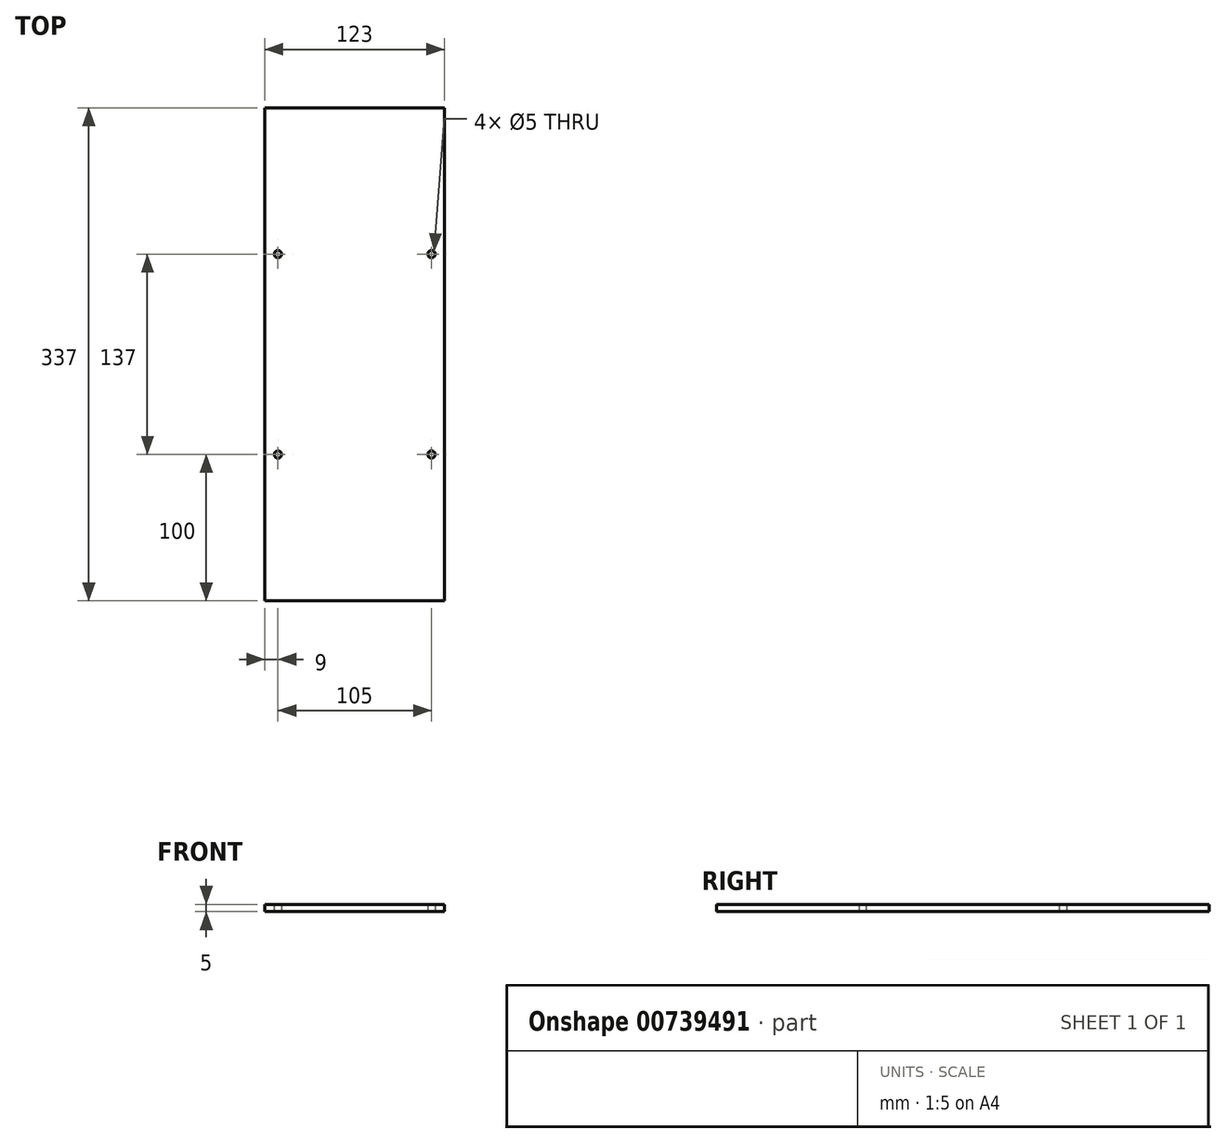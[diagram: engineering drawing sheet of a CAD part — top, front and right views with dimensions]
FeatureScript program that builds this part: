
annotation { "Feature Type Name" : "Feature", "Feature Type Description" : "" }
export const myFeature = defineFeature(function(context is Context, id is Id, definition is map)
    precondition{}
    {
        {
            var Q0;
            Q0=qCreatedBy(makeId("Top.planeOp"),FACE);
            var sketch = newSketch(context, id + "F0", { "sketchPlane" : qUnion([Q0])});
            skLineSegment(sketch, "E0.bottom", {"start": v(61.5, 168.5) * mm, "end": v(-61.5, 168.5) * mm});
            skLineSegment(sketch, "E0.top", {"start": v(61.5, -168.5) * mm, "end": v(-61.5, -168.5) * mm});
            skLineSegment(sketch, "E0.left", {"start": v(61.5, 168.5) * mm, "end": v(61.5, -168.5) * mm});
            skLineSegment(sketch, "E0.right", {"start": v(-61.5, 168.5) * mm, "end": v(-61.5, -168.5) * mm});
            skPoint(sketch, "E0.middle", {"position": v(0, 0) * mm});
            skLineSegment(sketch, "E1", {"start": v(0, 168.5) * mm, "end": v(0, -168.5) * mm, "construction": true});
            skCircle(sketch, "E2", {"center": v(-52.5, 68.5) * mm, "radius": 2.5 * mm});
            skCircle(sketch, "E3", {"center": v(-52.5, -68.5) * mm, "radius": 2.5 * mm});
            skCircle(sketch, "E4.MirrorC", {"center": v(52.5, -68.5) * mm, "radius": 2.5 * mm});
            skCircle(sketch, "E5.MirrorC", {"center": v(52.5, 68.5) * mm, "radius": 2.5 * mm});
            skSolve(sketch);
        }
        {
            var Q0;
            Q0=makeQuery(id+"F0.imprint","IMPRINT",FACE,{"disambiguationData":[TD([[makeQuery(id+"F0.imprint","IMPRINT",EDGE,{"derivedFrom":sQuery(id+"F0.wireOp",EDGE,"E0.bottom")}),1.0]])]});
            extrude(context, id + "F1", {"entities" : qUnion([Q0]), "depth" : 5 * mm, "offsetDistance" : 25 * mm});
        }
    });
